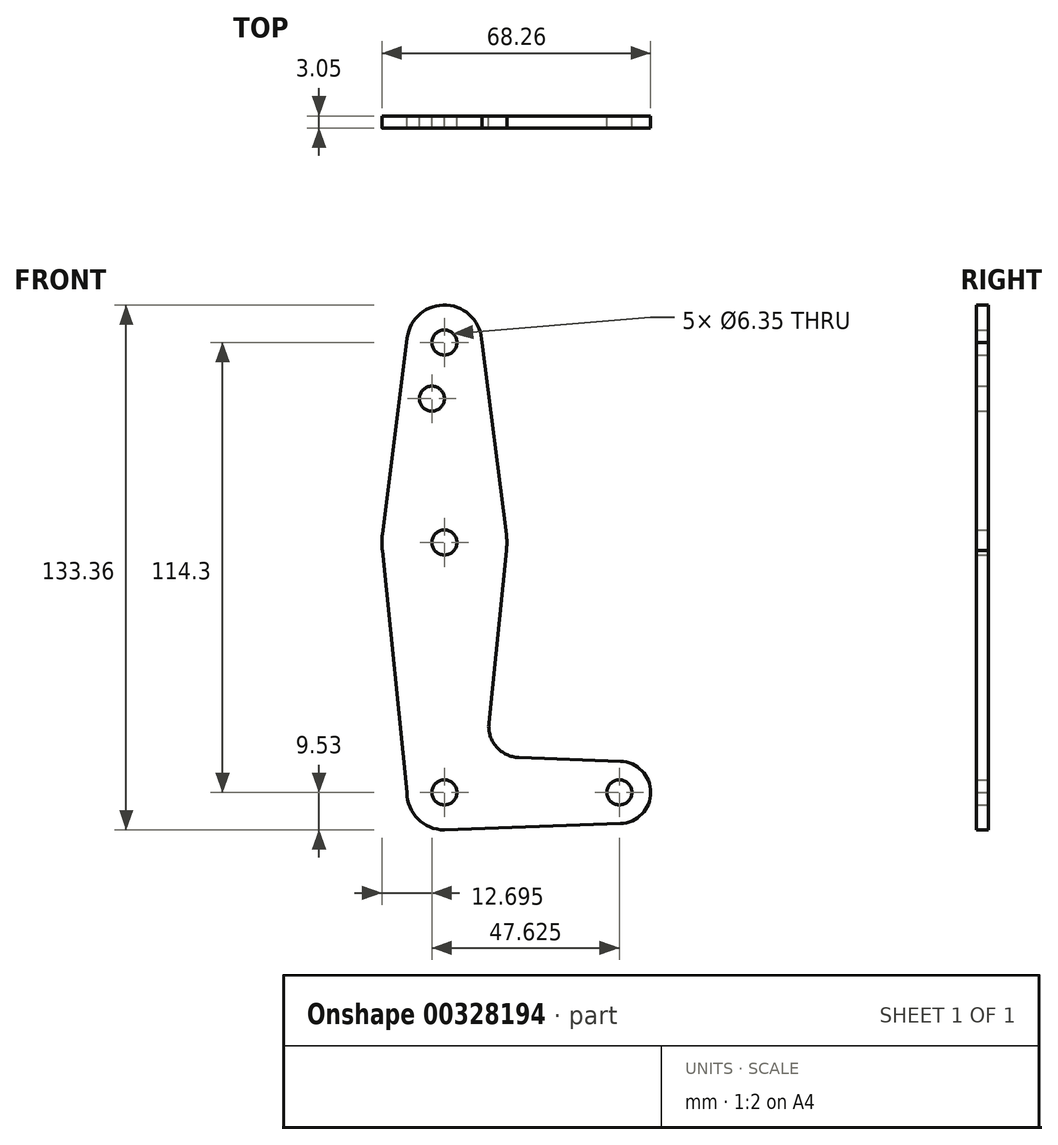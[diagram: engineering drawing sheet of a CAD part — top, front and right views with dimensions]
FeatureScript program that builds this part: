
annotation { "Feature Type Name" : "Feature", "Feature Type Description" : "" }
export const myFeature = defineFeature(function(context is Context, id is Id, definition is map)
    precondition{}
    {
        {
            var Q0;
            Q0=qCreatedBy(makeId("Front.planeOp"),FACE);
            var sketch = newSketch(context, id + "F0", { "sketchPlane" : qUnion([Q0])});
            skLineSegment(sketch, "E0", {"start": v(0, 0) * mm, "end": v(0, 114.3) * mm, "construction": true});
            skLineSegment(sketch, "E1", {"start": v(0, 0) * mm, "end": v(44.45, 0) * mm, "construction": true});
            skCircle(sketch, "E2", {"center": v(0, 114.3) * mm, "radius": 9.53 * mm});
            skCircle(sketch, "E3", {"center": v(44.45, 0) * mm, "radius": 7.94 * mm});
            skCircle(sketch, "E4", {"center": v(0, 0) * mm, "radius": 9.53 * mm});
            skCircle(sketch, "E5", {"center": v(0, 63.5) * mm, "radius": 15.88 * mm});
            skLineSegment(sketch, "E6", {"start": v(-9.45, 115.5) * mm, "end": v(-15.75, 65.48) * mm});
            skLineSegment(sketch, "E7", {"start": v(9.53, 114.3) * mm, "end": v(15.75, 65.5) * mm});
            skLineSegment(sketch, "E8", {"start": v(-9.53, 0) * mm, "end": v(-15.75, 61.52) * mm});
            skLineSegment(sketch, "E9", {"start": v(11.3, 17.6) * mm, "end": v(15.75, 61.5) * mm});
            skLineSegment(sketch, "E10", {"start": v(18.93, 8.85) * mm, "end": v(44.73, 7.93) * mm});
            skLineSegment(sketch, "E11", {"start": v(0, -9.53) * mm, "end": v(44.73, -7.93) * mm});
            skCircle(sketch, "E12", {"center": v(0, 114.3) * mm, "radius": 3.18 * mm});
            skCircle(sketch, "E13", {"center": v(0, 63.5) * mm, "radius": 3.18 * mm});
            skCircle(sketch, "E14", {"center": v(0, 0) * mm, "radius": 3.18 * mm});
            skCircle(sketch, "E15", {"center": v(44.45, 0) * mm, "radius": 3.18 * mm});
            skCircle(sketch, "E16", {"center": v(-3.18, 100.03) * mm, "radius": 3.18 * mm});
            skArc(sketch, "E17.filletArc", {"start": v(11.3, 17.6) * mm, "mid": v(13.22, 11.57) * mm, "end": v(18.93, 8.85) * mm});
            skSolve(sketch);
        }
        {
            var Q0;
            Q0=makeQuery(id+"F0.imprint","IMPRINT",FACE,{"disambiguationData":[TD([[makeQuery(id+"F0.imprint","IMPRINT",EDGE,{"derivedFrom":sQuery(id+"F0.wireOp",EDGE,"E12")}),-1.0]])]});
            var Q1;
            {var subQ1=sQuery(id+"F0.wireOp",EDGE,"E6");Q1=makeQuery(id+"F0.imprint","IMPRINT",FACE,{"disambiguationData":[TD([[makeQuery(id+"F0.imprint","IMPRINT",EDGE,{"derivedFrom":subQ1}),1.0]])]});}
            var Q2;
            Q2=makeQuery(id+"F0.imprint","IMPRINT",FACE,{"disambiguationData":[TD([[makeQuery(id+"F0.imprint","IMPRINT",EDGE,{"derivedFrom":sQuery(id+"F0.wireOp",EDGE,"E13")}),-1.0]])]});
            var Q3;
            Q3=makeQuery(id+"F0.imprint","IMPRINT",FACE,{"disambiguationData":[TD([[makeQuery(id+"F0.imprint","IMPRINT",EDGE,{"derivedFrom":sQuery(id+"F0.wireOp",EDGE,"E14")}),-1.0]])]});
            var Q4;
            Q4=makeQuery(id+"F0.imprint","IMPRINT",FACE,{"disambiguationData":[TD([[makeQuery(id+"F0.imprint","IMPRINT",EDGE,{"derivedFrom":sQuery(id+"F0.wireOp",EDGE,"E15")}),-1.0]])]});
            var Q5;
            {var subQ0=sQuery(id+"F0.wireOp",EDGE,"E8");Q5=makeQuery(id+"F0.imprint","IMPRINT",FACE,{"disambiguationData":[TD([[makeQuery(id+"F0.imprint","IMPRINT",EDGE,{"derivedFrom":subQ0}),-1.0]])]});}
            extrude(context, id + "F1", {"entities" : qUnion([Q0, Q1, Q2, Q3, Q4, Q5]), "depth" : 3.05 * mm});
        }
    });
